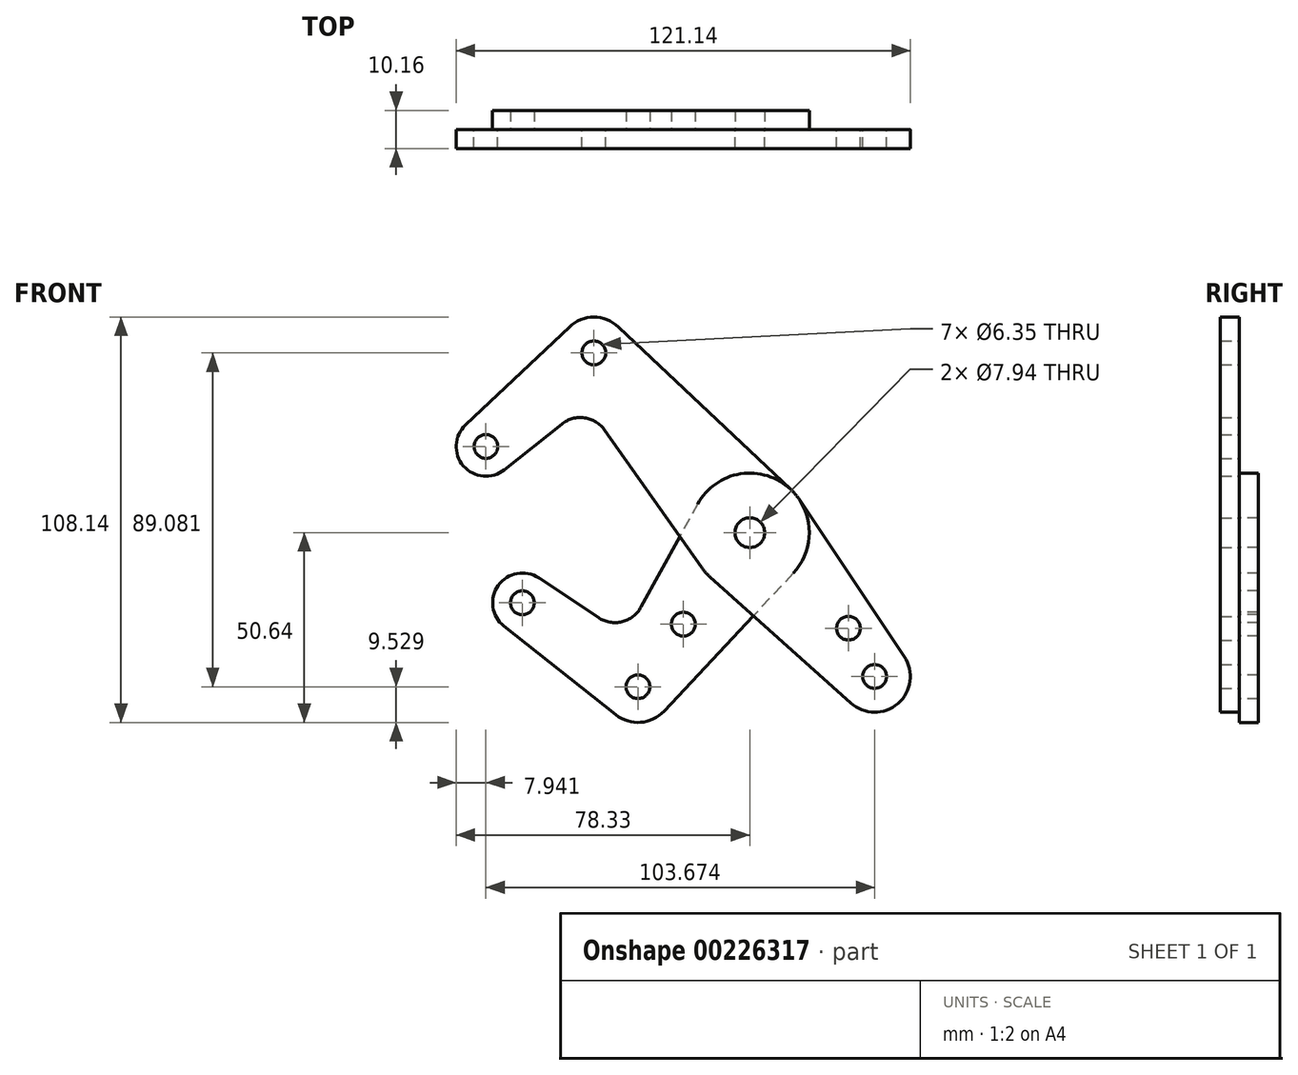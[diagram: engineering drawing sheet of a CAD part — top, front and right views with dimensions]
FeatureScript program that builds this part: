
annotation { "Feature Type Name" : "Feature", "Feature Type Description" : "" }
export const myFeature = defineFeature(function(context is Context, id is Id, definition is map)
    precondition{}
    {
        {
            var Q0;
            Q0=qCreatedBy(makeId("Front.planeOp"),FACE);
            var sketch = newSketch(context, id + "F0", { "sketchPlane" : qUnion([Q0])});
            skLineSegment(sketch, "E0", {"start": v(-41.6, 47.97) * mm, "end": v(41.6, -47.97) * mm, "construction": true});
            skCircle(sketch, "E1", {"center": v(0, 0) * mm, "radius": 3.18 * mm});
            skCircle(sketch, "E2", {"center": v(33.29, -38.38) * mm, "radius": 3.18 * mm});
            skCircle(sketch, "E3", {"center": v(-41.6, 47.97) * mm, "radius": 3.18 * mm});
            skCircle(sketch, "E4", {"center": v(-70.39, 23) * mm, "radius": 3.18 * mm});
            skLineSegment(sketch, "E5", {"start": v(-41.6, 47.97) * mm, "end": v(-70.39, 23) * mm, "construction": true});
            skCircle(sketch, "E6", {"center": v(33.29, -38.38) * mm, "radius": 9.53 * mm});
            skCircle(sketch, "E7", {"center": v(-70.39, 23) * mm, "radius": 7.94 * mm});
            skCircle(sketch, "E8", {"center": v(-41.6, 47.97) * mm, "radius": 9.53 * mm});
            skLineSegment(sketch, "E9", {"start": v(-75.83, 28.78) * mm, "end": v(-48.14, 54.9) * mm});
            skLineSegment(sketch, "E10", {"start": v(-65.44, 16.8) * mm, "end": v(-50.15, 28.98) * mm});
            skCircle(sketch, "E11", {"center": v(0, 0) * mm, "radius": 15.88 * mm});
            skLineSegment(sketch, "E12", {"start": v(-35.07, 54.9) * mm, "end": v(10.9, 11.55) * mm});
            skLineSegment(sketch, "E13", {"start": v(-38.72, 27.35) * mm, "end": v(-12.97, -9.15) * mm});
            skLineSegment(sketch, "E14", {"start": v(-10.6, -11.82) * mm, "end": v(26.93, -45.47) * mm});
            skLineSegment(sketch, "E15", {"start": v(13.2, 8.82) * mm, "end": v(41.2, -33.08) * mm});
            skArc(sketch, "E16.filletArc", {"start": v(-38.72, 27.35) * mm, "mid": v(-44.08, 30.63) * mm, "end": v(-50.15, 28.98) * mm});
            skLineSegment(sketch, "E17", {"start": v(0, 0) * mm, "end": v(-29.84, -41.11) * mm, "construction": true});
            skLineSegment(sketch, "E18", {"start": v(-29.84, -41.11) * mm, "end": v(-60.68, -18.73) * mm, "construction": true});
            skCircle(sketch, "E19", {"center": v(-60.68, -18.73) * mm, "radius": 3.18 * mm});
            skCircle(sketch, "E20", {"center": v(-29.84, -41.11) * mm, "radius": 3.18 * mm});
            skCircle(sketch, "E21", {"center": v(-60.68, -18.73) * mm, "radius": 7.94 * mm});
            skCircle(sketch, "E22", {"center": v(-29.84, -41.11) * mm, "radius": 9.53 * mm});
            skLineSegment(sketch, "E23", {"start": v(-56.28, -12.12) * mm, "end": v(-40.4, -22.67) * mm});
            skLineSegment(sketch, "E24", {"start": v(-65.6, -24.95) * mm, "end": v(-35.75, -48.58) * mm});
            skLineSegment(sketch, "E25", {"start": v(-13.91, 7.65) * mm, "end": v(-29.04, -19.88) * mm});
            skLineSegment(sketch, "E26", {"start": v(11.58, -10.86) * mm, "end": v(-22.9, -47.63) * mm});
            skArc(sketch, "E27.filletArc", {"start": v(-40.4, -22.67) * mm, "mid": v(-34.1, -23.77) * mm, "end": v(-29.04, -19.88) * mm});
            skCircle(sketch, "E28", {"center": v(-17.72, -24.4) * mm, "radius": 3.18 * mm});
            skCircle(sketch, "E29", {"center": v(26.32, -25.5) * mm, "radius": 3.18 * mm});
            skLineSegment(sketch, "E30", {"start": v(26.32, -25.5) * mm, "end": v(23.92, -27.58) * mm, "construction": true});
            skCircle(sketch, "E31", {"center": v(0, 0) * mm, "radius": 3.97 * mm});
            skSolve(sketch);
        }
        {
            var Q0;
            {var subQ1=sQuery(id+"F0.wireOp",EDGE,"E9");Q0=makeQuery(id+"F0.imprint","IMPRINT",FACE,{"disambiguationData":[TD([[makeQuery(id+"F0.imprint","IMPRINT",EDGE,{"derivedFrom":subQ1}),-1.0]])]});}
            var Q1;
            Q1=makeQuery(id+"F0.imprint","IMPRINT",FACE,{"disambiguationData":[TD([[makeQuery(id+"F0.imprint","IMPRINT",EDGE,{"derivedFrom":sQuery(id+"F0.wireOp",EDGE,"E4")}),-1.0]])]});
            var Q2;
            Q2=makeQuery(id+"F0.imprint","IMPRINT",FACE,{"disambiguationData":[TD([[makeQuery(id+"F0.imprint","IMPRINT",EDGE,{"derivedFrom":sQuery(id+"F0.wireOp",EDGE,"E3")}),-1.0]])]});
            var Q3;
            Q3=makeQuery(id+"F0.imprint","IMPRINT",FACE,{"disambiguationData":[TD([[makeQuery(id+"F0.imprint","IMPRINT",EDGE,{"derivedFrom":sQuery(id+"F0.wireOp",EDGE,"E31")}),-1.0]])]});
            var Q4;
            {var subQ0=sQuery(id+"F0.wireOp",EDGE,"E14");var subQ1=sQuery(id+"F0.wireOp",EDGE,"E11");var subQ2=makeQuery(id+"F0.imprint","INTERSECT",VERTEX,{"derivedFrom":[subQ1,subQ0]});Q4=makeQuery(id+"F0.imprint","IMPRINT",FACE,{"disambiguationData":[TD([[makeQuery(id+"F0.imprint","IMPRINT",EDGE,{"disambiguationData":[TD([[subQ2,-1.0]])],"derivedFrom":subQ1}),-1.0]])]});}
            var Q5;
            {var subQ0=sQuery(id+"F0.wireOp",EDGE,"E13");var subQ1=sQuery(id+"F0.wireOp",EDGE,"E11");var subQ2=makeQuery(id+"F0.imprint","INTERSECT",VERTEX,{"derivedFrom":[subQ1,subQ0]});Q5=makeQuery(id+"F0.imprint","IMPRINT",FACE,{"disambiguationData":[TD([[makeQuery(id+"F0.imprint","IMPRINT",EDGE,{"disambiguationData":[TD([[subQ2,1.0]])],"derivedFrom":subQ1}),-1.0]])]});}
            var Q6;
            {var subQ0=sQuery(id+"F0.wireOp",EDGE,"E15");Q6=makeQuery(id+"F0.imprint","IMPRINT",FACE,{"disambiguationData":[TD([[makeQuery(id+"F0.imprint","IMPRINT",EDGE,{"derivedFrom":subQ0}),-1.0]])]});}
            var Q7;
            Q7=makeQuery(id+"F0.imprint","IMPRINT",FACE,{"disambiguationData":[TD([[makeQuery(id+"F0.imprint","IMPRINT",EDGE,{"derivedFrom":sQuery(id+"F0.wireOp",EDGE,"E2")}),-1.0]])]});
            extrude(context, id + "F1", {"entities" : qUnion([Q0, Q1, Q2, Q3, Q4, Q5, Q6, Q7]), "depth" : 5.08 * mm});
        }
        {
            var Q0;
            Q0=makeQuery(id+"F0.imprint","IMPRINT",FACE,{"disambiguationData":[TD([[makeQuery(id+"F0.imprint","IMPRINT",EDGE,{"derivedFrom":sQuery(id+"F0.wireOp",EDGE,"E31")}),-1.0]])]});
            var Q1;
            {var subQ0=sQuery(id+"F0.wireOp",EDGE,"E14");var subQ1=sQuery(id+"F0.wireOp",EDGE,"E11");var subQ2=makeQuery(id+"F0.imprint","INTERSECT",VERTEX,{"derivedFrom":[subQ1,subQ0]});Q1=makeQuery(id+"F0.imprint","IMPRINT",FACE,{"disambiguationData":[TD([[makeQuery(id+"F0.imprint","IMPRINT",EDGE,{"disambiguationData":[TD([[subQ2,-1.0]])],"derivedFrom":subQ1}),-1.0]])]});}
            var Q2;
            {var subQ0=sQuery(id+"F0.wireOp",EDGE,"E13");var subQ1=sQuery(id+"F0.wireOp",EDGE,"E11");var subQ2=makeQuery(id+"F0.imprint","INTERSECT",VERTEX,{"derivedFrom":[subQ1,subQ0]});Q2=makeQuery(id+"F0.imprint","IMPRINT",FACE,{"disambiguationData":[TD([[makeQuery(id+"F0.imprint","IMPRINT",EDGE,{"disambiguationData":[TD([[subQ2,1.0]])],"derivedFrom":subQ1}),-1.0]])]});}
            var Q3;
            {var subQ10=sQuery(id+"F0.wireOp",EDGE,"E23");Q3=makeQuery(id+"F0.imprint","IMPRINT",FACE,{"disambiguationData":[TD([[makeQuery(id+"F0.imprint","IMPRINT",EDGE,{"derivedFrom":subQ10}),-1.0]])]});}
            var Q4;
            Q4=makeQuery(id+"F0.imprint","IMPRINT",FACE,{"disambiguationData":[TD([[makeQuery(id+"F0.imprint","IMPRINT",EDGE,{"derivedFrom":sQuery(id+"F0.wireOp",EDGE,"E20")}),-1.0]])]});
            var Q5;
            Q5=makeQuery(id+"F0.imprint","IMPRINT",FACE,{"disambiguationData":[TD([[makeQuery(id+"F0.imprint","IMPRINT",EDGE,{"derivedFrom":sQuery(id+"F0.wireOp",EDGE,"E19")}),-1.0]])]});
            extrude(context, id + "F2", {"entities" : qUnion([Q0, Q1, Q2, Q3, Q4, Q5]), "oppositeDirection" : true, "depth" : 5.08 * mm});
        }
    });
